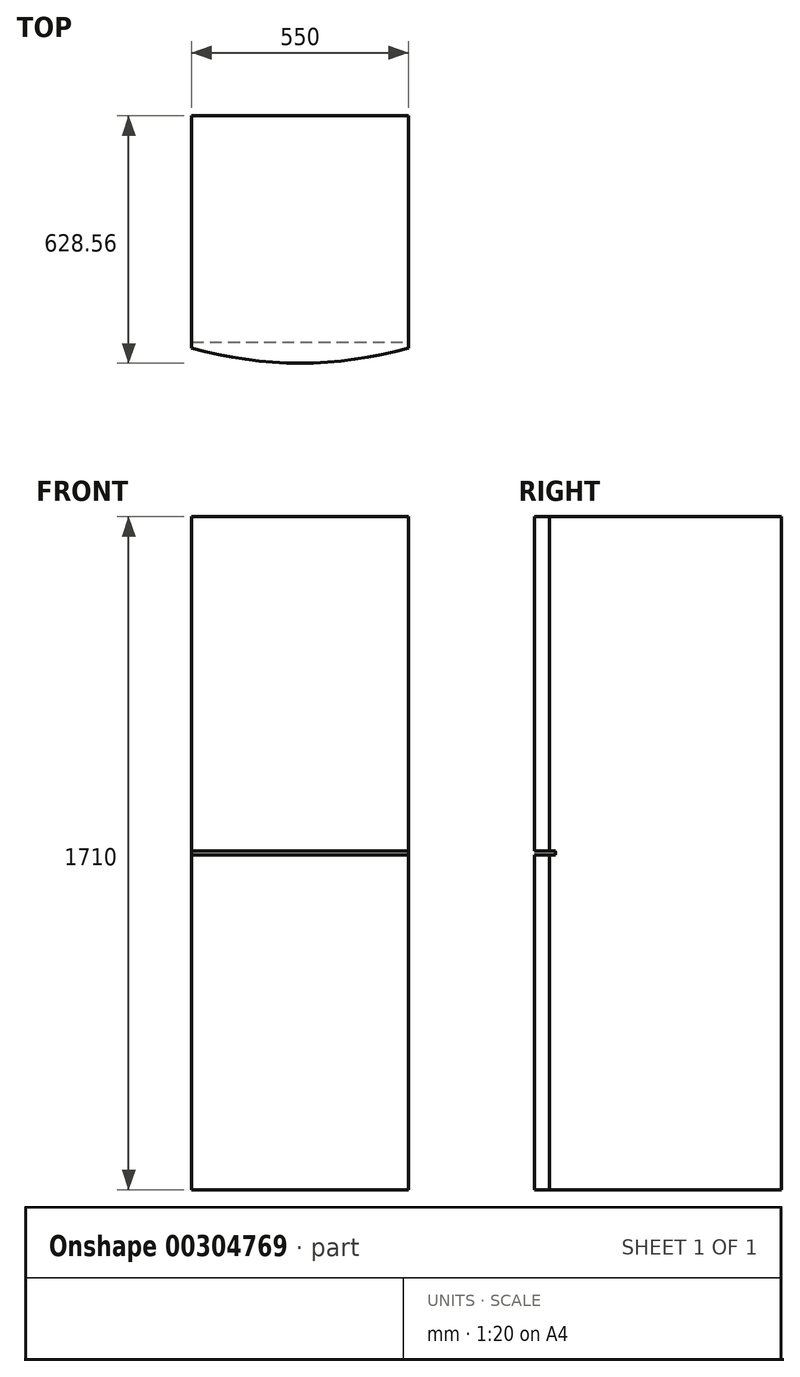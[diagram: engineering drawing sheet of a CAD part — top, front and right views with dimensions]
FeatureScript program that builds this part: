
annotation { "Feature Type Name" : "Feature", "Feature Type Description" : "" }
export const myFeature = defineFeature(function(context is Context, id is Id, definition is map)
    precondition{}
    {
        {
            var Q0;
            Q0=qCreatedBy(makeId("Top.planeOp"),FACE);
            var sketch = newSketch(context, id + "F0", { "sketchPlane" : qUnion([Q0])});
            skLineSegment(sketch, "E0", {"start": v(-277.06, -167.25) * mm, "end": v(-277.06, 422.75) * mm});
            skLineSegment(sketch, "E1", {"start": v(-277.06, 422.75) * mm, "end": v(272.94, 422.75) * mm});
            skLineSegment(sketch, "E2", {"start": v(272.94, 422.75) * mm, "end": v(272.94, -167.25) * mm});
            skArc(sketch, "E3", {"start": v(-277.06, -167.25) * mm, "mid": v(-2.06, -205.8) * mm, "end": v(272.94, -167.25) * mm});
            skSolve(sketch);
        }
        {
            var Q0;
            Q0=makeQuery(id+"F0.imprint","IMPRINT",FACE,{"disambiguationData":[TD([[makeQuery(id+"F0.imprint","IMPRINT",EDGE,{"derivedFrom":sQuery(id+"F0.wireOp",EDGE,"E0")}),-1.0]])]});
            extrude(context, id + "F1", {"entities" : qUnion([Q0]), "depth" : 850 * mm});
        }
        {
            var Q0;
            Q0=makeQuery(id+"F1.opExtrude","CAP_FACE",FACE,{"disambiguationData":[OSD([sQuery(id+"F0.wireOp",EDGE,"E0"),sQuery(id+"F0.wireOp",EDGE,"E1"),sQuery(id+"F0.wireOp",EDGE,"E2"),sQuery(id+"F0.wireOp",EDGE,"E3")])],"isStart":false});
            var sketch = newSketch(context, id + "F2", { "sketchPlane" : qUnion([Q0])});
            skLineSegment(sketch, "E4.0", {"start": v(-277.06, -152.25) * mm, "end": v(-277.06, 422.75) * mm});
            skLineSegment(sketch, "E5.0", {"start": v(-277.06, 422.75) * mm, "end": v(272.94, 422.75) * mm});
            skLineSegment(sketch, "E6.0", {"start": v(272.94, 422.75) * mm, "end": v(272.94, -152.25) * mm});
            skLineSegment(sketch, "E7", {"start": v(-277.06, -152.25) * mm, "end": v(272.94, -152.25) * mm});
            skPoint(sketch, "E8.orphan", {"position": v(-277.06, -167.25) * mm});
            skPoint(sketch, "E9.orphan", {"position": v(272.94, -167.25) * mm});
            skSolve(sketch);
        }
        {
            var Q0;
            Q0=makeQuery(id+"F2.imprint","IMPRINT",FACE,{"disambiguationData":[TD([[makeQuery(id+"F2.imprint","IMPRINT",EDGE,{"derivedFrom":sQuery(id+"F2.wireOp",EDGE,"E4.0")}),-1.0]])]});
            extrude(context, id + "F3", {"entities" : qUnion([Q0]), "operationType" : NewBodyOperationType.ADD, "depth" : 10 * mm});
        }
        {
            var Q0;
            Q0=makeQuery(id+"F3.opExtrude","CAP_FACE",FACE,{"disambiguationData":[OSD([sQuery(id+"F2.wireOp",EDGE,"E4.0"),sQuery(id+"F2.wireOp",EDGE,"E5.0"),sQuery(id+"F2.wireOp",EDGE,"E6.0"),sQuery(id+"F2.wireOp",EDGE,"E7")])],"isStart":false});
            var sketch = newSketch(context, id + "F4", { "sketchPlane" : qUnion([Q0])});
            skLineSegment(sketch, "E10.0", {"start": v(-277.06, -152.25) * mm, "end": v(-277.06, 422.75) * mm});
            skLineSegment(sketch, "E11.0", {"start": v(-277.06, 422.75) * mm, "end": v(272.94, 422.75) * mm});
            skLineSegment(sketch, "E12.0", {"start": v(272.94, 422.75) * mm, "end": v(272.94, -152.25) * mm});
            skArc(sketch, "E13.0", {"start": v(-277.06, -167.25) * mm, "mid": v(-2.06, -205.8) * mm, "end": v(272.94, -167.25) * mm});
            skPoint(sketch, "E14.0", {"position": v(272.94, -159.75) * mm});
            skLineSegment(sketch, "E15.0", {"start": v(-277.06, -167.25) * mm, "end": v(-277.06, -152.25) * mm});
            skLineSegment(sketch, "E16.0", {"start": v(272.94, -152.25) * mm, "end": v(272.94, -167.25) * mm});
            skSolve(sketch);
        }
        {
            var Q0;
            Q0=makeQuery(id+"F4.imprint","IMPRINT",FACE,{"disambiguationData":[TD([[makeQuery(id+"F4.imprint","IMPRINT",EDGE,{"derivedFrom":sQuery(id+"F4.wireOp",EDGE,"E10.0")}),-1.0]])]});
            var Q1;
            Q1=makeQuery(id+"F4.imprint","IMPRINT",FACE,{"disambiguationData":[TD([[makeQuery(id+"F4.imprint","IMPRINT",EDGE,{"derivedFrom":sQuery(id+"F4.wireOp",EDGE,"E13.0")}),1.0]])]});
            extrude(context, id + "F5", {"entities" : qUnion([Q0, Q1]), "operationType" : NewBodyOperationType.ADD, "depth" : 850 * mm});
        }
    });
